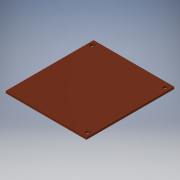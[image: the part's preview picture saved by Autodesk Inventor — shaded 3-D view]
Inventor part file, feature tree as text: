
AUTODESK INVENTOR PART (.ipt)
format: ipt  version: 2019 (Build 230136000, 136)  size: 107,008 bytes
history: native  units: mm
features: sketch x2, extrude x1, hole x1
ambient origin geometry x8: Origin, YZ Plane, XZ Plane, XY Plane, X Axis, Y Axis, Z Axis, Center Point
bodies: Solid1 (feature_tree)
feature tree (4):
  extrude  "Extrusion1"  Depth=77.47mm
  hole  "Hole1"  [1 undecoded]
  sketch  "Sketch1"  dims[d0=71.12mm d1=77.47mm]
  sketch  "Sketch2"  dims[d2=1.6mm d3=0.0mm d4=68.58mm d5=64.516mm d6=3.4mm d7=6.0mm d8=6.3mm d9=2.0mm d10=90.0deg d11=8.0mm d12=20.594885mm]
note: 1 required parameter value undecoded (feature->parameter linkage not recoverable at this tier; creation-order binding heuristic only, values carry confidence <= 0.55)
